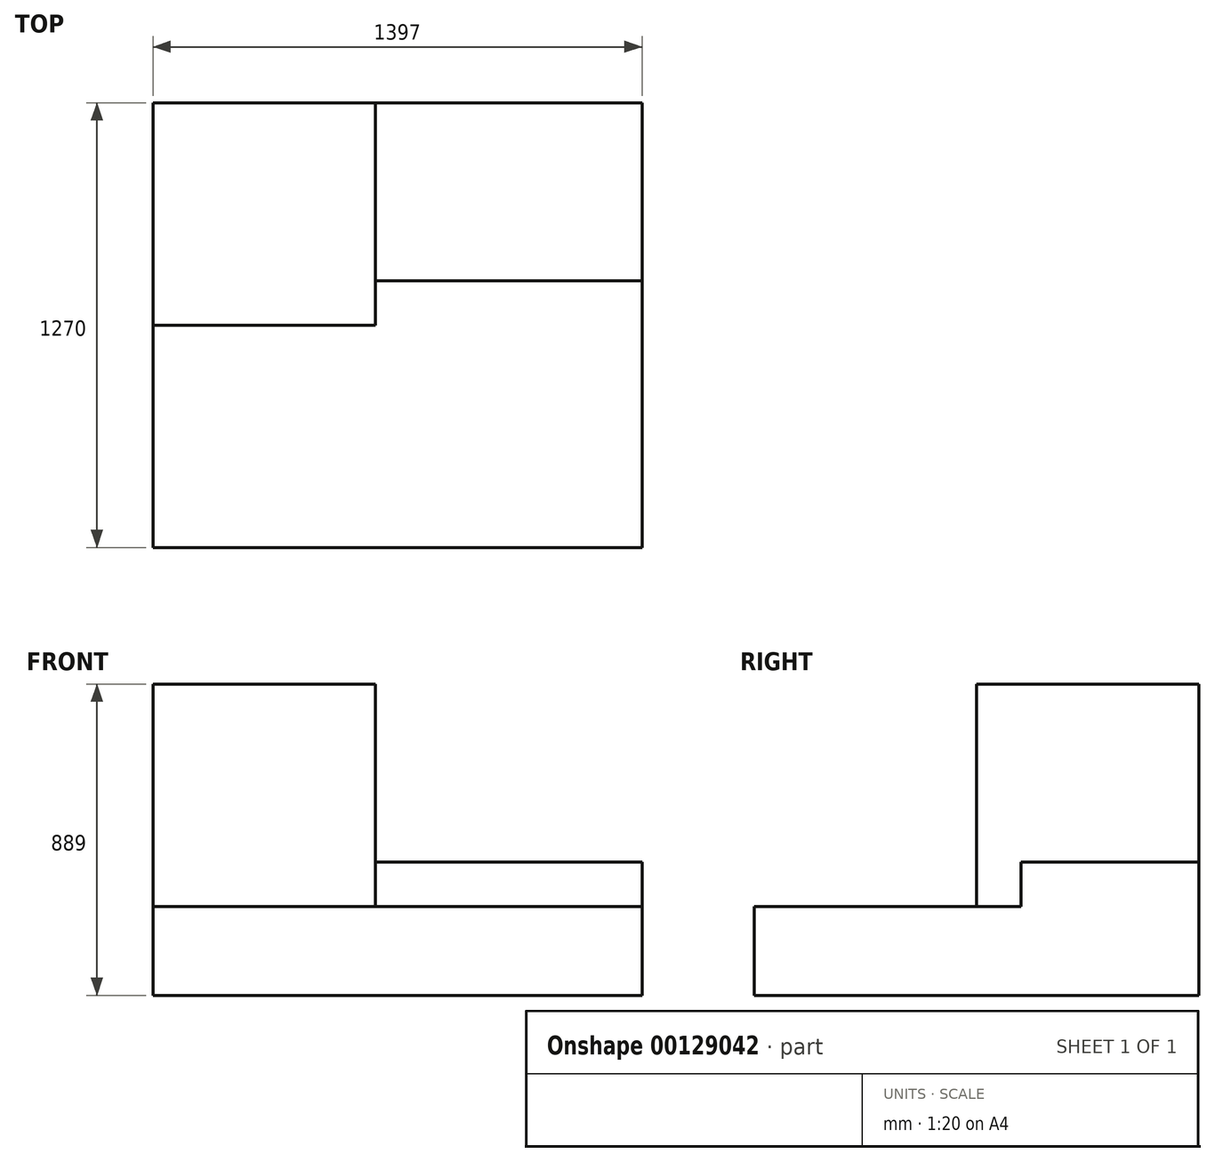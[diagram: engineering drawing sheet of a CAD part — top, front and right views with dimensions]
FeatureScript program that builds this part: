
annotation { "Feature Type Name" : "Feature", "Feature Type Description" : "" }
export const myFeature = defineFeature(function(context is Context, id is Id, definition is map)
    precondition{}
    {
        {
            var Q0;
            Q0=qCreatedBy(makeId("Front.planeOp"),FACE);
            var sketch = newSketch(context, id + "F0", { "sketchPlane" : qUnion([Q0])});
            skLineSegment(sketch, "E0.bottom", {"start": v(-698.5, 444.5) * mm, "end": v(698.5, 444.5) * mm});
            skLineSegment(sketch, "E0.top", {"start": v(-698.5, -444.5) * mm, "end": v(698.5, -444.5) * mm});
            skLineSegment(sketch, "E0.left", {"start": v(-698.5, 444.5) * mm, "end": v(-698.5, -444.5) * mm});
            skLineSegment(sketch, "E0.right", {"start": v(698.5, 444.5) * mm, "end": v(698.5, -444.5) * mm});
            skPoint(sketch, "E0.middle", {"position": v(0, 0) * mm});
            skSolve(sketch);
        }
        {
            var Q0;
            Q0=makeQuery(id+"F0.imprint","IMPRINT",FACE,{"disambiguationData":[TD([[makeQuery(id+"F0.imprint","IMPRINT",EDGE,{"derivedFrom":sQuery(id+"F0.wireOp",EDGE,"E0.bottom")}),-1.0]])]});
            extrude(context, id + "F1", {"entities" : qUnion([Q0]), "depth" : 1270 * mm});
        }
        {
            var Q0;
            Q0=makeQuery(id+"F1.opExtrude","SWEPT_FACE",FACE,{"disambiguationData":[OSD([sQuery(id+"F0.wireOp",EDGE,"E0.right")])]});
            var sketch = newSketch(context, id + "F2", { "sketchPlane" : qUnion([Q0])});
            skLineSegment(sketch, "E1", {"start": v(-635, 444.5) * mm, "end": v(-635, -190.5) * mm});
            skLineSegment(sketch, "E2", {"start": v(-635, -190.5) * mm, "end": v(-1270, -190.5) * mm});
            skLineSegment(sketch, "E3", {"start": v(-1270, -190.5) * mm, "end": v(-1270, 444.5) * mm});
            skLineSegment(sketch, "E4", {"start": v(-1270, 444.5) * mm, "end": v(-635, 444.5) * mm});
            skSolve(sketch);
        }
        {
            var Q0;
            Q0=makeQuery(id+"F2.imprint","IMPRINT",FACE,{"disambiguationData":[TD([[makeQuery(id+"F2.imprint","IMPRINT",EDGE,{"derivedFrom":sQuery(id+"F2.wireOp",EDGE,"E1")}),-1.0]])]});
            extrude(context, id + "F3", {"entities" : qUnion([Q0]), "operationType" : NewBodyOperationType.REMOVE, "endBound" : BoundingType.THROUGH_ALL, "oppositeDirection" : true, "depth" : 25.4 * mm});
        }
        {
            var Q0;
            Q0=makeQuery(id+"F3.boolean.opBoolean","COPY",FACE,{"derivedFrom":makeQuery(id+"F3.opExtrude","SWEPT_FACE",FACE,{"disambiguationData":[OSD([sQuery(id+"F2.wireOp",EDGE,"E1")])]})});
            var sketch = newSketch(context, id + "F4", { "sketchPlane" : qUnion([Q0])});
            skLineSegment(sketch, "E5", {"start": v(-63.5, 444.5) * mm, "end": v(-63.5, -63.5) * mm});
            skLineSegment(sketch, "E6", {"start": v(-63.5, -63.5) * mm, "end": v(698.5, -63.5) * mm});
            skLineSegment(sketch, "E7", {"start": v(698.5, -63.5) * mm, "end": v(698.5, 444.5) * mm});
            skLineSegment(sketch, "E8", {"start": v(698.5, 444.5) * mm, "end": v(-63.5, 444.5) * mm});
            skSolve(sketch);
        }
        {
            var Q0;
            Q0=makeQuery(id+"F4.imprint","IMPRINT",FACE,{"disambiguationData":[TD([[makeQuery(id+"F4.imprint","IMPRINT",EDGE,{"derivedFrom":sQuery(id+"F4.wireOp",EDGE,"E5")}),1.0]])]});
            extrude(context, id + "F5", {"entities" : qUnion([Q0]), "operationType" : NewBodyOperationType.REMOVE, "endBound" : BoundingType.THROUGH_ALL, "oppositeDirection" : true, "depth" : 25.4 * mm});
        }
        {
            var Q0;
            Q0=makeQuery(id+"F3.boolean.opBoolean","COPY",FACE,{"derivedFrom":makeQuery(id+"F3.opExtrude","SWEPT_FACE",FACE,{"disambiguationData":[OSD([sQuery(id+"F2.wireOp",EDGE,"E1")])]})});
            var sketch = newSketch(context, id + "F6", { "sketchPlane" : qUnion([Q0])});
            skLineSegment(sketch, "E9", {"start": v(-63.5, -63.5) * mm, "end": v(-63.5, -190.5) * mm});
            skLineSegment(sketch, "E10", {"start": v(-63.5, -190.5) * mm, "end": v(698.5, -190.5) * mm});
            skLineSegment(sketch, "E11", {"start": v(698.5, -190.5) * mm, "end": v(698.5, -63.5) * mm});
            skLineSegment(sketch, "E12", {"start": v(698.5, -63.5) * mm, "end": v(-63.5, -63.5) * mm});
            skSolve(sketch);
        }
        {
            var Q0;
            Q0=makeQuery(id+"F6.imprint","IMPRINT",FACE,{"disambiguationData":[TD([[makeQuery(id+"F6.imprint","IMPRINT",EDGE,{"derivedFrom":sQuery(id+"F6.wireOp",EDGE,"E9")}),1.0]])]});
            extrude(context, id + "F7", {"entities" : qUnion([Q0]), "operationType" : NewBodyOperationType.REMOVE, "oppositeDirection" : true, "depth" : 127 * mm});
        }
    });
